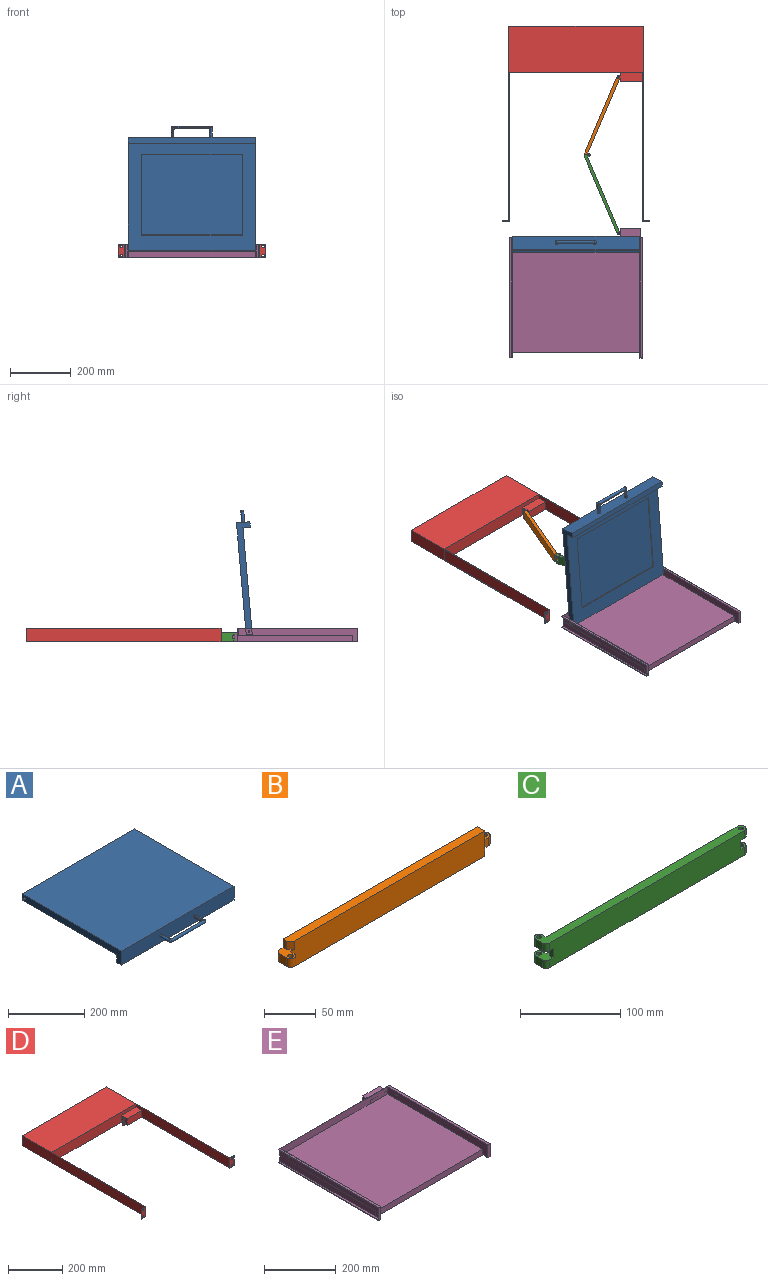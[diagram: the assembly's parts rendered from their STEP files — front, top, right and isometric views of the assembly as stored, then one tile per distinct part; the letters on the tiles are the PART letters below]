
ASSEMBLY  parts=5 mates=5
PART A: 39 faces, bbox 428x409x44.5 mm
  f0: plane 2x2mm, normal (0,0,1), area 1.8mm2, adj f25,f27,f36
  f1: plane 2x2mm, normal (0,0,1), area 1.8mm2, adj f27,f29,f32
  f2: plane 418x351mm, normal (0,0,-1), area 58074mm2, adj f3,f4,f6,f8,f14,f15,f16,f17
  f3: plane 418x20mm, normal (0,1,0), area 8360mm2, adj f2,f4,f6,f7
  f4: plane 369x44.5mm, normal (-1,0,0), area 7801.4mm2, adj f2,f3,f5,f7,f8,f9,f12
  f5: plane 418x44.5mm, normal (0,-1,0), area 18470.1mm2, adj f4,f6,f7,f9,f19,f20,f22,f25
  f6: plane 369x44.5mm, normal (1,0,0), area 7801.4mm2, adj f2,f3,f5,f7,f8,f9,f11
  f7: plane 418x369mm, normal (0,0,1), area 154242mm2, adj f3,f4,f5,f6
  f8: plane 418x24.5mm, normal (0,1,0), area 10241mm2, adj f2,f4,f6,f9
  f9: plane 418x18mm, normal (0,0,-1), area 7524mm2, adj f4,f5,f6,f8
  f10: plane 5x5mm, normal (1,0,0), area 19.6mm2, adj f11
  f11: cylinder r=2.5mm len=5mm, axis (-1,0,0), area 78.5mm2, adj f6,f10
  f12: cylinder r=2.5mm len=5mm, axis (-1,0,0), area 78.5mm2, adj f4,f13
  f13: plane 5x5mm, normal (-1,0,0), area 19.6mm2, adj f12
  f14: plane 332x3mm, normal (0,1,0), area 996mm2, adj f2,f15,f17,f18
  f15: plane 267x3mm, normal (1,0,0), area 801mm2, adj f2,f14,f16,f18
  f16: plane 332x3mm, normal (0,-1,0), area 996mm2, adj f2,f15,f17,f18
  f17: plane 267x3mm, normal (-1,0,0), area 801mm2, adj f2,f14,f16,f18
  f18: plane 332x267mm, normal (0,0,-1), area 88644mm2, adj f14,f15,f16,f17
  f19: plane 125x35mm, normal (0,0,-1), area 577.7mm2, adj f5,f20,f21,f22,f23,f24,f25,f27
  f20: plane 27x5.42mm, normal (1,0,0), area 146.3mm2, adj f5,f19,f23,f30
  f21: plane 109x5.42mm, normal (0,1,0), area 590.5mm2, adj f19,f23,f24,f34
  f22: plane 27x5.42mm, normal (-1,0,0), area 146.3mm2, adj f5,f19,f24,f38
  f23: cylinder r=5mm len=5.42mm, axis (0,0,-1), area 40.6mm2, adj f19,f20,f21,f31,f32,f33
  f24: cylinder r=5mm len=5.42mm, axis (0,0,1), area 40.6mm2, adj f19,f21,f22,f35,f36,f37
  f25: cylinder r=5mm len=35mm, axis (0,1,0), area 549.8mm2, adj f0,f5,f19,f26,f37,f38
  f26: sphere r=5mm, area 78.5mm2, adj f25,f27
  f27: cylinder r=5mm len=125mm, axis (1,0,0), area 1963.5mm2, adj f0,f1,f19,f26,f28,f33,f34,f35
  f28: sphere r=5mm, area 78.5mm2, adj f27,f29
  f29: cylinder r=5mm len=35mm, axis (0,-1,0), area 549.8mm2, adj f1,f5,f19,f28,f30,f31
  f30: cylinder r=5mm len=27mm, axis (0,1,0), area 156.5mm2, adj f5,f20,f29,f31
  f31: bspline ~7.26x5.45mm, area 26.2mm2, adj f23,f29,f30,f32
  f32: torus R=10mm, axis (0,0,-1), area 15.2mm2, adj f1,f23,f31,f33
  f33: bspline ~7.01x5.3mm, area 26.2mm2, adj f23,f27,f32,f34
  f34: cylinder r=5mm len=109mm, axis (-1,0,0), area 631.8mm2, adj f21,f27,f33,f35
  f35: bspline ~7.01x5.3mm, area 26.2mm2, adj f24,f27,f34,f36
  f36: torus R=10mm, axis (0,0,-1), area 15.2mm2, adj f0,f24,f35,f37
  f37: bspline ~7.26x5.45mm, area 26.2mm2, adj f24,f25,f36,f38
  f38: cylinder r=5mm len=27mm, axis (0,1,0), area 156.5mm2, adj f5,f22,f25,f37
PART B: 23 faces, bbox 285x20x30 mm
  f0: plane 10x10mm, normal (1,0,0), area 100mm2, adj f3,f6,f9,f16
  f1: plane 10x10mm, normal (-1,0,0), area 100mm2, adj f4,f5,f10,f12
  f2: plane 10x5mm, normal (1,0,0), area 50mm2, adj f5,f9,f10,f12
  f3: plane 270x30mm, normal (0,1,0), area 8000mm2, adj f0,f4,f6,f7,f8,f10,f11,f12
  f4: cylinder r=5mm len=10mm, axis (0,0,-1), area 78.5mm2, adj f1,f3,f10,f12
  f5: cylinder r=5mm len=10mm, axis (0,0,-1), area 157.1mm2, adj f1,f2,f10,f12
  f6: plane 265x10mm, normal (0,0,1), area 2637.5mm2, adj f0,f3,f9,f13,f22
  f7: plane 265x10mm, normal (0,0,-1), area 2637.5mm2, adj f3,f8,f9,f11,f21
  f8: plane 10x10mm, normal (1,0,0), area 100mm2, adj f3,f7,f9,f15
  f9: plane 265x30mm, normal (0,-1,0), area 7850mm2, adj f0,f2,f6,f7,f8,f10,f12,f18
  f10: plane 20x15mm, normal (0,0,-1), area 176.8mm2, adj f1,f2,f3,f4,f5,f9,f11,f14
  f11: plane 10x5mm, normal (-1,0,0), area 50mm2, adj f3,f7,f10,f21
  f12: plane 20x15mm, normal (0,0,1), area 176.8mm2, adj f1,f2,f3,f4,f5,f9,f13,f14
  f13: plane 10x5mm, normal (-1,0,0), area 50mm2, adj f3,f6,f12,f22
  f14: cylinder r=2.5mm len=10mm, axis (0,0,-1), area 157.1mm2, adj f10,f12
  f15: plane 10x10mm, normal (0,0,-1), area 69.6mm2, adj f8,f17,f18,f19,f20
  f16: plane 10x10mm, normal (0,0,1), area 69.6mm2, adj f0,f17,f18,f19,f20
  f17: plane 10x5mm, normal (0,1,0), area 50mm2, adj f3,f15,f16,f19
  f18: plane 10x5mm, normal (0,-1,0), area 50mm2, adj f9,f15,f16,f19
  f19: cylinder r=5mm len=10mm, axis (0,0,-1), area 157.1mm2, adj f15,f16,f17,f18
  f20: cylinder r=2.5mm len=10mm, axis (0,0,1), area 157.1mm2, adj f15,f16
  f21: plane 10x5mm, normal (-0.71,-0.71,0), area 70.7mm2, adj f7,f9,f10,f11
  f22: plane 10x5mm, normal (-0.71,-0.71,0), area 70.7mm2, adj f6,f9,f12,f13
PART C: 27 faces, bbox 285x20x30 mm
  f0: plane 11x10mm, normal (1,0,0), area 110mm2, adj f3,f7,f18,f20
  f1: plane 9.5x5mm, normal (1,0,0), area 47.5mm2, adj f7,f9,f13,f16
  f2: plane 10x9.5mm, normal (-1,0,0), area 95mm2, adj f9,f12,f13,f16
  f3: plane 275x30mm, normal (0,-1,0), area 8140mm2, adj f0,f6,f12,f13,f14,f15,f16,f17
  f4: cylinder r=5mm len=10mm, axis (0,0,-1), area 149.2mm2, adj f8,f10,f14,f15
  f5: cylinder r=2.5mm len=9.5mm, axis (0,0,-1), area 149.2mm2, adj f14,f15
  f6: cylinder r=5mm len=9.5mm, axis (0,0,-1), area 74.6mm2, adj f3,f10,f14,f15
  f7: plane 265x30mm, normal (0,1,0), area 7895mm2, adj f0,f1,f8,f13,f14,f15,f16,f19
  f8: plane 9.5x5mm, normal (1,0,0), area 47.5mm2, adj f4,f7,f14,f15
  f9: cylinder r=5mm len=10mm, axis (0,0,-1), area 149.2mm2, adj f1,f2,f13,f16
  f10: plane 10x9.5mm, normal (-1,0,0), area 95mm2, adj f4,f6,f14,f15
  f11: cylinder r=2.5mm len=9.5mm, axis (0,0,-1), area 149.2mm2, adj f13,f16
  f12: cylinder r=5mm len=9.5mm, axis (0,0,-1), area 74.6mm2, adj f2,f3,f13,f16
  f13: plane 285x20mm, normal (0,0,1), area 2883.9mm2, adj f1,f2,f3,f7,f9,f11,f12,f19
  f14: plane 285x20mm, normal (0,0,-1), area 2883.9mm2, adj f3,f4,f5,f6,f7,f8,f10,f21
  f15: plane 20x15mm, normal (0,0,1), area 176.8mm2, adj f3,f4,f5,f6,f7,f8,f10,f17
  f16: plane 20x15mm, normal (0,0,-1), area 176.8mm2, adj f1,f2,f3,f7,f9,f11,f12,f17
  f17: plane 11x5mm, normal (-1,0,0), area 55mm2, adj f3,f15,f16,f26
  f18: plane 10x10mm, normal (0,0,-1), area 69.6mm2, adj f0,f3,f19,f23,f25
  f19: plane 9.5x5mm, normal (0,1,0), area 47.5mm2, adj f7,f13,f18,f23
  f20: plane 10x10mm, normal (0,0,1), area 69.6mm2, adj f0,f3,f21,f22,f24
  f21: plane 9.5x5mm, normal (0,1,0), area 47.5mm2, adj f7,f14,f20,f22
  f22: cylinder r=5mm len=10mm, axis (0,0,-1), area 149.2mm2, adj f3,f14,f20,f21
  f23: cylinder r=5mm len=10mm, axis (0,0,-1), area 149.2mm2, adj f3,f13,f18,f19
  f24: cylinder r=2.5mm len=9.5mm, axis (0,0,1), area 149.2mm2, adj f14,f20
  f25: cylinder r=2.5mm len=9.5mm, axis (0,0,1), area 149.2mm2, adj f13,f18
  f26: plane 11x5mm, normal (-0.71,0.71,0), area 77.8mm2, adj f7,f15,f16,f17
PART D: 43 faces, bbox 483x643x44.5 mm
  f0: plane 643x483mm, normal (0,0,-1), area 71454.4mm2, adj f1,f2,f3,f6,f7,f8,f9,f10
  f1: plane 44.5x20.5mm, normal (0,1,0), area 793.3mm2, adj f0,f7,f8,f14,f34,f35,f36,f37
  f2: plane 44.5x22.5mm, normal (0,-1,0), area 882.3mm2, adj f0,f8,f9,f14,f34,f35,f36,f37
  f3: plane 44.5x21.5mm, normal (0,-1,0), area 837.8mm2, adj f0,f10,f11,f14,f26,f27,f28,f29
  f4: plane 9.5x5mm, normal (0,1,0), area 47.5mm2, adj f15,f19,f21,f23
  f5: plane 9.5x5mm, normal (0,-1,0), area 47.5mm2, adj f15,f19,f21,f23
  f6: plane 439x44.5mm, normal (0,-1,0), area 17285.5mm2, adj f0,f9,f10,f14,f15,f19
  f7: plane 642x44.5mm, normal (-1,0,0), area 28569mm2, adj f0,f1,f14,f42
  f8: plane 44.5x1mm, normal (-1,0,0), area 44.5mm2, adj f0,f1,f2,f14
  f9: plane 490.01x44.5mm, normal (1,0,0), area 21805.2mm2, adj f0,f2,f6,f14
  f10: plane 490x44.5mm, normal (-1,0,0), area 20905mm2, adj f0,f3,f6,f14,f18,f19
  f11: plane 44.5x1mm, normal (1,0,0), area 44.5mm2, adj f0,f3,f12,f14
  f12: plane 44.5x20.5mm, normal (0,1,0), area 793.3mm2, adj f0,f11,f13,f14,f26,f27,f28,f29
  f13: plane 642x44.5mm, normal (1,0,0), area 28569mm2, adj f0,f12,f14,f42
  f14: plane 643x483mm, normal (0,0,1), area 69134.7mm2, adj f1,f2,f3,f6,f7,f8,f9,f10
  f15: plane 30x30mm, normal (-1,0,0), area 710mm2, adj f0,f4,f5,f6,f16,f17,f18,f19
  f16: plane 9.5x5mm, normal (0,1,0), area 47.5mm2, adj f0,f15,f20,f22
  f17: plane 9.5x5mm, normal (0,-1,0), area 47.5mm2, adj f0,f15,f20,f22
  f18: plane 75x30mm, normal (0,-1,0), area 2250mm2, adj f0,f10,f15,f19
  f19: plane 85x30mm, normal (0,0,1), area 2319.6mm2, adj f4,f5,f6,f10,f15,f18,f23,f24
  f20: plane 10x10mm, normal (0,0,1), area 69.6mm2, adj f15,f16,f17,f22,f25
  f21: plane 10x10mm, normal (0,0,-1), area 69.6mm2, adj f4,f5,f15,f23,f24
  f22: cylinder r=5mm len=10mm, axis (0,0,1), area 149.2mm2, adj f0,f16,f17,f20
  f23: cylinder r=5mm len=10mm, axis (0,0,1), area 149.2mm2, adj f4,f5,f19,f21
  f24: cylinder r=2.5mm len=9.5mm, axis (0,0,1), area 149.2mm2, adj f19,f21
  f25: cylinder r=2.5mm len=9.5mm, axis (0,0,1), area 149.2mm2, adj f0,f20
  f26: cylinder r=3.5mm len=7mm, axis (0,-1,0), area 11mm2, adj f3,f12,f27,f29
  f27: plane 3x1mm, normal (0,0,1), area 3mm2, adj f3,f12,f26,f28
  f28: cylinder r=3.5mm len=7mm, axis (0,-1,0), area 11mm2, adj f3,f12,f27,f29
  f29: plane 3x1mm, normal (0,0,-1), area 3mm2, adj f3,f12,f26,f28
  f30: plane 3x1mm, normal (0,0,-1), area 3mm2, adj f3,f12,f31,f33
  f31: cylinder r=3.5mm len=7mm, axis (0,-1,0), area 11mm2, adj f3,f12,f30,f32
  f32: plane 3x1mm, normal (0,0,1), area 3mm2, adj f3,f12,f31,f33
  f33: cylinder r=3.5mm len=7mm, axis (0,-1,0), area 11mm2, adj f3,f12,f30,f32
  f34: cylinder r=3.5mm len=7mm, axis (0,-1,0), area 11mm2, adj f1,f2,f35,f37
  f35: plane 3x1mm, normal (0,0,1), area 3mm2, adj f1,f2,f34,f36
  f36: cylinder r=3.5mm len=7mm, axis (0,-1,0), area 11mm2, adj f1,f2,f35,f37
  f37: plane 3x1mm, normal (0,0,-1), area 3mm2, adj f1,f2,f34,f36
  f38: plane 3x1mm, normal (0,0,-1), area 3mm2, adj f1,f2,f39,f41
  f39: cylinder r=3.5mm len=7mm, axis (0,-1,0), area 11mm2, adj f1,f2,f38,f40
  f40: plane 3x1mm, normal (0,0,1), area 3mm2, adj f1,f2,f39,f41
  f41: cylinder r=3.5mm len=7mm, axis (0,-1,0), area 11mm2, adj f1,f2,f38,f40
  f42: plane 442x44.5mm, normal (0,1,0), area 19669mm2, adj f0,f7,f13,f14
PART E: 34 faces, bbox 437x426x44.5 mm
  f0: plane 437x44.5mm, normal (0,1,0), area 16885.5mm2, adj f1,f3,f8,f10,f15,f16,f25,f27
  f1: plane 396.01x44.5mm, normal (-1,0,0), area 1250.3mm2, adj f0,f8,f13,f15,f29,f30,f31
  f2: cylinder r=2.75mm len=5.5mm, axis (-1,0,0), area 17.3mm2, adj f5,f32
  f3: plane 396.01x44.5mm, normal (1,0,0), area 1250.3mm2, adj f0,f8,f12,f15,f25,f26,f27
  f4: cylinder r=2.75mm len=5.5mm, axis (-1,0,0), area 34.6mm2, adj f11,f28
  f5: plane 395.01x44.5mm, normal (1,0,0), area 10033.9mm2, adj f2,f8,f13,f14,f15,f23,f24
  f6: plane 10x5mm, normal (0,-1,0), area 50mm2, adj f16,f18,f19,f21
  f7: plane 10x0mm, normal (-1,0,0), area 0mm2, adj f18,f19,f20,f21
  f8: plane 437x426.01mm, normal (0,0,-1), area 167054.2mm2, adj f0,f1,f3,f5,f11,f12,f13,f16
  f9: plane 10x5mm, normal (0,1,0), area 50mm2, adj f16,f18,f19,f20
  f10: plane 66x30mm, normal (0,0,1), area 1980mm2, adj f0,f16,f17,f33
  f11: plane 395.01x44.5mm, normal (-1,0,0), area 10033.9mm2, adj f4,f8,f12,f14,f15,f23,f24
  f12: plane 44.5x9mm, normal (0,-1,0), area 400.5mm2, adj f3,f8,f11,f15
  f13: plane 44.5x8mm, normal (0,-1,0), area 356mm2, adj f1,f5,f8,f15
  f14: plane 420x24.5mm, normal (0,-1,0), area 10290mm2, adj f5,f11,f15,f24
  f15: plane 437x396.01mm, normal (0,0,1), area 7152.1mm2, adj f0,f1,f3,f5,f11,f12,f13,f14
  f16: plane 30x30mm, normal (-1,0,0), area 800mm2, adj f0,f6,f8,f9,f10,f17,f18,f19
  f17: plane 66x30mm, normal (0,1,0), area 1980mm2, adj f8,f10,f16,f33
  f18: plane 10x10mm, normal (0,0,-1), area 69.6mm2, adj f6,f7,f9,f16,f20,f21,f22
  f19: plane 10x10mm, normal (0,0,1), area 69.6mm2, adj f6,f7,f9,f16,f20,f21,f22
  f20: cylinder r=5mm len=10mm, axis (0,0,1), area 78.5mm2, adj f7,f9,f18,f19
  f21: cylinder r=5mm len=10mm, axis (0,0,-1), area 78.5mm2, adj f6,f7,f18,f19
  f22: cylinder r=2.5mm len=10mm, axis (0,0,1), area 157.1mm2, adj f18,f19
  f23: plane 420x20mm, normal (0,-1,0), area 8400mm2, adj f5,f8,f11,f24
  f24: plane 420x376.01mm, normal (0,0,1), area 157922.1mm2, adj f5,f11,f14,f23
  f25: plane 394.51x7mm, normal (0,0,-1), area 2761.5mm2, adj f0,f3,f26,f28
  f26: plane 41.5x7mm, normal (0,1,0), area 290.5mm2, adj f3,f25,f27,f28
  f27: plane 394.51x7mm, normal (0,0,1), area 2761.5mm2, adj f0,f3,f26,f28
  f28: plane 394.51x41.5mm, normal (1,0,0), area 16348.2mm2, adj f0,f4,f25,f26,f27
  f29: plane 394.51x7mm, normal (0,0,1), area 2761.5mm2, adj f0,f1,f30,f32
  f30: plane 41.5x7mm, normal (0,1,0), area 290.5mm2, adj f1,f29,f31,f32
  f31: plane 394.51x7mm, normal (0,0,-1), area 2761.5mm2, adj f0,f1,f30,f32
  f32: plane 394.51x41.5mm, normal (-1,0,0), area 16348.2mm2, adj f0,f2,f29,f30,f31
  f33: plane 30x30mm, normal (1,0,0), area 900mm2, adj f0,f8,f10,f17
PLACE A rot(axis=(-1,0,0),95deg) t=(4.49,-362.46,108.75)mm
PLACE B rot(axis=(0,0,1),67deg) t=(315.54,-33.63,-1.62)mm
PLACE C rot(axis=(0,0,-1),67deg) t=(26.28,-140.25,-1.62)mm
PLACE D t=(4.99,42.38,-1.62)mm fixed
PLACE E t=(4.99,-407.62,-1.62)mm
MATE revolute B.f19 <-> D.f22  axis (0,0,-1) through (222.71,231.54,8.38)mm
MATE revolute E.f21 <-> C.f22  axis (0,0,1) through (222.71,-282.46,18.38)mm
MATE slider E.f13 <-> D.f2  axis (0,-1,0) through (-131.29,-693.47,42.88)mm
MATE revolute A.f11 <-> E.f2  axis (-1,0,0) through (-126.79,-334.47,32.88)mm
MATE revolute C.f4 <-> B.f5  axis (0,0,-1) through (124.35,-25.46,18.88)mm
